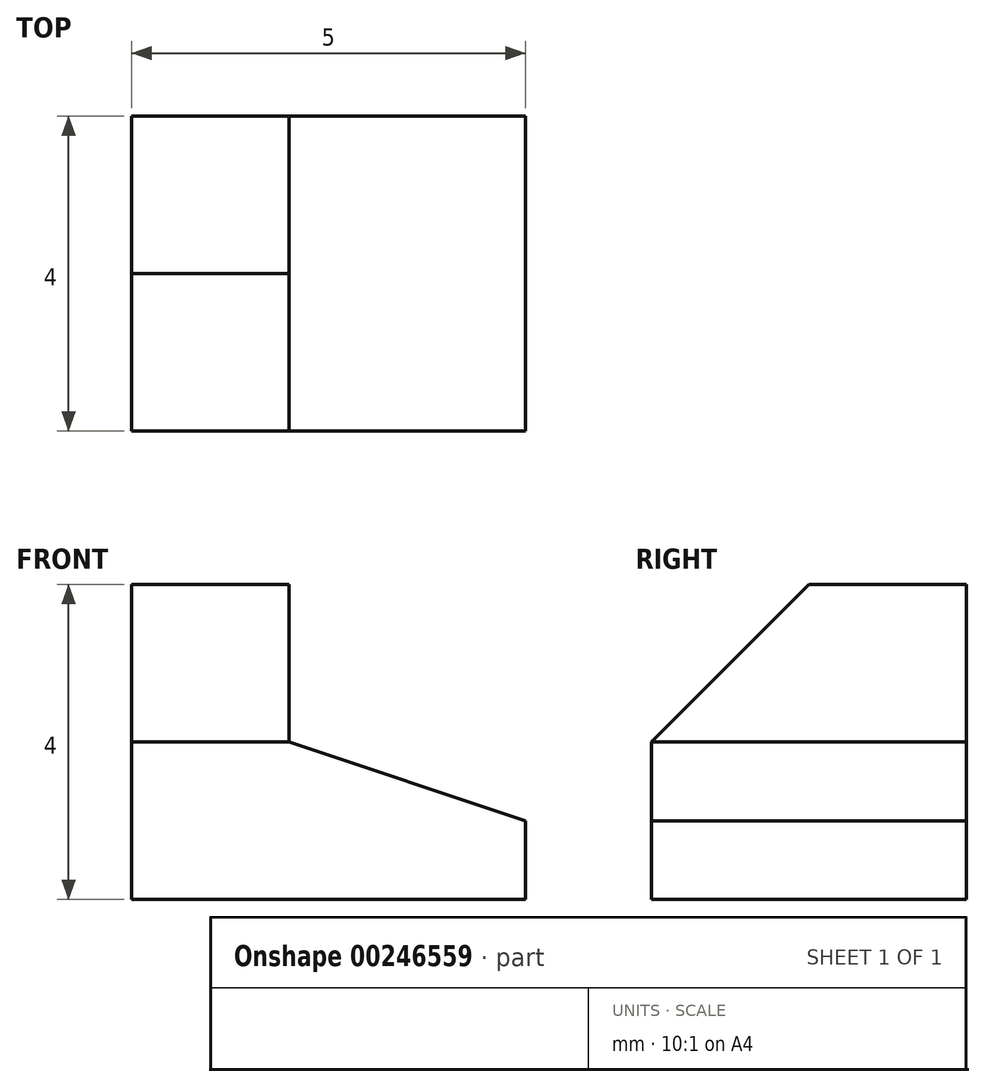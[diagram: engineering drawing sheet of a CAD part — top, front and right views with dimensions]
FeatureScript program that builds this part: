
annotation { "Feature Type Name" : "Feature", "Feature Type Description" : "" }
export const myFeature = defineFeature(function(context is Context, id is Id, definition is map)
    precondition{}
    {
        {
            var Q0;
            Q0=qCreatedBy(makeId("Top.planeOp"),FACE);
            var sketch = newSketch(context, id + "F0", { "sketchPlane" : qUnion([Q0])});
            skLineSegment(sketch, "E0.bottom", {"start": v(0, 0) * mm, "end": v(5, 0) * mm});
            skLineSegment(sketch, "E0.top", {"start": v(0, 4) * mm, "end": v(5, 4) * mm});
            skLineSegment(sketch, "E0.left", {"start": v(0, 0) * mm, "end": v(0, 4) * mm});
            skLineSegment(sketch, "E0.right", {"start": v(5, 0) * mm, "end": v(5, 4) * mm});
            skSolve(sketch);
        }
        {
            var Q0;
            Q0=makeQuery(id+"F0.imprint","IMPRINT",FACE,{"disambiguationData":[TD([[makeQuery(id+"F0.imprint","IMPRINT",EDGE,{"derivedFrom":sQuery(id+"F0.wireOp",EDGE,"E0.bottom")}),1.0]])]});
            extrude(context, id + "F1", {"entities" : qUnion([Q0]), "depth" : 2 * mm});
        }
        {
            var Q0;
            Q0=makeQuery(id+"F1.opExtrude","SWEPT_FACE",FACE,{"disambiguationData":[OSD([sQuery(id+"F0.wireOp",EDGE,"E0.bottom")])]});
            var sketch = newSketch(context, id + "F2", { "sketchPlane" : qUnion([Q0])});
            skLineSegment(sketch, "E1", {"start": v(5, 2) * mm, "end": v(5, 1) * mm});
            skLineSegment(sketch, "E2", {"start": v(5, 2) * mm, "end": v(2, 2) * mm});
            skLineSegment(sketch, "E3", {"start": v(2, 2) * mm, "end": v(5, 1) * mm});
            skSolve(sketch);
        }
        {
            var Q0;
            Q0=makeQuery(id+"F2.imprint","IMPRINT",FACE,{"disambiguationData":[TD([[makeQuery(id+"F2.imprint","IMPRINT",EDGE,{"derivedFrom":sQuery(id+"F2.wireOp",EDGE,"E1")}),-1.0]])]});
            extrude(context, id + "F3", {"entities" : qUnion([Q0]), "operationType" : NewBodyOperationType.REMOVE, "oppositeDirection" : true, "depth" : 25 * mm});
        }
        {
            var Q0;
            Q0=makeQuery(id+"F1.opExtrude","CAP_FACE",FACE,{"disambiguationData":[OSD([sQuery(id+"F0.wireOp",EDGE,"E0.bottom"),sQuery(id+"F0.wireOp",EDGE,"E0.top"),sQuery(id+"F0.wireOp",EDGE,"E0.left"),sQuery(id+"F0.wireOp",EDGE,"E0.right")])],"isStart":false});
            var sketch = newSketch(context, id + "F4", { "sketchPlane" : qUnion([Q0])});
            skSolve(sketch);
        }
        {
            var Q0;
            Q0=makeQuery(id+"F4.imprint","IMPRINT",FACE,{"disambiguationData":[TD([[makeQuery(id+"F4.imprint","IMPRINT",EDGE,{"derivedFrom":makeQuery(id+"F1.opExtrude","CAP_EDGE",EDGE,{"disambiguationData":[OSD([sQuery(id+"F0.wireOp",EDGE,"E0.left")])],"isStart":false})}),-1.0]])]});
            extrude(context, id + "F5", {"entities" : qUnion([Q0]), "operationType" : NewBodyOperationType.ADD, "depth" : 2 * mm});
        }
        {
            var Q0;
            {var subQ0=sQuery(id+"F0.wireOp",EDGE,"E0.left");Q0=makeQuery(id+"F5.boolean.opBoolean","MERGE",FACE,{"derivedFrom":[makeQuery(id+"F1.opExtrude","SWEPT_FACE",FACE,{"disambiguationData":[OSD([subQ0])]}),makeQuery(id+"F5.opExtrude","SWEPT_FACE",FACE,{"disambiguationData":[OSD([subQ0])]})]});}
            var sketch = newSketch(context, id + "F6", { "sketchPlane" : qUnion([Q0])});
            skLineSegment(sketch, "E4.bottom", {"start": v(-2, 4) * mm, "end": v(0, 4) * mm});
            skLineSegment(sketch, "E4.top", {"start": v(-2, 2) * mm, "end": v(0, 2) * mm});
            skLineSegment(sketch, "E4.left", {"start": v(-2, 4) * mm, "end": v(-2, 2) * mm});
            skLineSegment(sketch, "E4.right", {"start": v(0, 4) * mm, "end": v(0, 2) * mm});
            skLineSegment(sketch, "E5", {"start": v(-2, 4) * mm, "end": v(0, 2) * mm});
            skSolve(sketch);
        }
        {
            var Q0;
            Q0=makeQuery(id+"F6.imprint","IMPRINT",FACE,{"disambiguationData":[TD([[makeQuery(id+"F6.imprint","IMPRINT",EDGE,{"derivedFrom":sQuery(id+"F6.wireOp",EDGE,"E4.bottom")}),1.0]])]});
            extrude(context, id + "F7", {"entities" : qUnion([Q0]), "operationType" : NewBodyOperationType.REMOVE, "oppositeDirection" : true, "depth" : 25 * mm});
        }
    });
